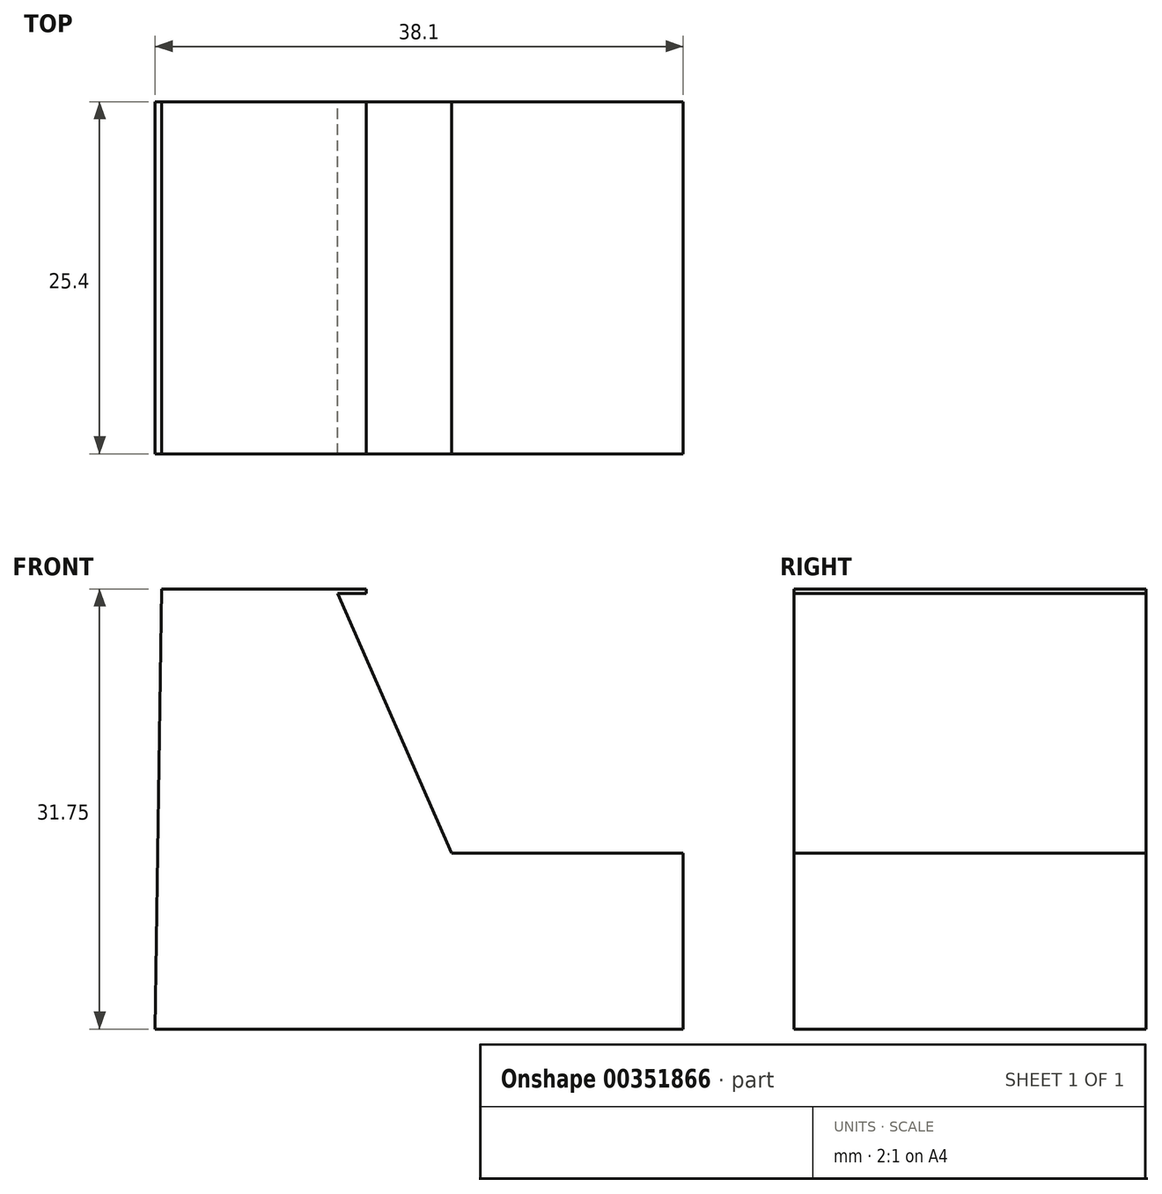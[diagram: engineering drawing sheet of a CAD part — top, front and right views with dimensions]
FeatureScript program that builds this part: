
annotation { "Feature Type Name" : "Feature", "Feature Type Description" : "" }
export const myFeature = defineFeature(function(context is Context, id is Id, definition is map)
    precondition{}
    {
        {
            var Q0;
            Q0=qCreatedBy(makeId("Front.planeOp"),FACE);
            var sketch = newSketch(context, id + "F0", { "sketchPlane" : qUnion([Q0])});
            skLineSegment(sketch, "E0", {"start": v(-38.1, 0) * mm, "end": v(0, 0) * mm});
            skLineSegment(sketch, "E1", {"start": v(0, 0) * mm, "end": v(0, 31.75) * mm});
            skLineSegment(sketch, "E2", {"start": v(0, 31.75) * mm, "end": v(-37.63, 31.75) * mm});
            skLineSegment(sketch, "E3", {"start": v(-37.63, 31.75) * mm, "end": v(-38.1, 0) * mm});
            skSolve(sketch);
        }
        {
            var Q0;
            Q0=makeQuery(id+"F0.imprint","IMPRINT",FACE,{"disambiguationData":[TD([[makeQuery(id+"F0.imprint","IMPRINT",EDGE,{"derivedFrom":sQuery(id+"F0.wireOp",EDGE,"E0")}),1.0]])]});
            var sketch = newSketch(context, id + "F1", { "sketchPlane" : qUnion([Q0])});
            skLineSegment(sketch, "E4", {"start": v(-24.93, 31.4) * mm, "end": v(-16.7, 12.7) * mm});
            skLineSegment(sketch, "E5", {"start": v(-16.7, 12.7) * mm, "end": v(0, 12.7) * mm});
            skLineSegment(sketch, "E6", {"start": v(-24.93, 31.4) * mm, "end": v(0, 31.4) * mm});
            skLineSegment(sketch, "E7", {"start": v(0, 31.4) * mm, "end": v(0, 12.7) * mm});
            skSolve(sketch);
        }
        {
            var Q0;
            Q0=makeQuery(id+"F1.imprint","IMPRINT",FACE,{"disambiguationData":[TD([[makeQuery(id+"F1.imprint","IMPRINT",EDGE,{"derivedFrom":sQuery(id+"F1.wireOp",EDGE,"E4")}),-1.0]])]});
            extrude(context, id + "F2", {"entities" : qUnion([Q0]), "depth" : 25.4 * mm});
        }
        {
            var Q0;
            Q0=makeQuery(id+"F2.opExtrude","SWEPT_FACE",FACE,{"disambiguationData":[OSD([sQuery(id+"F0.wireOp",EDGE,"E2")])]});
            var sketch = newSketch(context, id + "F3", { "sketchPlane" : qUnion([Q0])});
            skLineSegment(sketch, "E8", {"start": v(-22.86, 0) * mm, "end": v(-22.86, -35.47) * mm});
            skLineSegment(sketch, "E9", {"start": v(-22.86, 0) * mm, "end": v(0, 0) * mm});
            skLineSegment(sketch, "E10", {"start": v(0, 0) * mm, "end": v(0, -28.09) * mm});
            skLineSegment(sketch, "E11", {"start": v(-22.86, -25.4) * mm, "end": v(0, -25.4) * mm});
            skPoint(sketch, "E11.startSnap0", {"position": v(-18.81, -25.4) * mm});
            skSolve(sketch);
        }
        {
            var Q0;
            {var subQ0=sQuery(id+"F3.wireOp",EDGE,"E9");Q0=makeQuery(id+"F3.imprint","IMPRINT",FACE,{"disambiguationData":[TD([[makeQuery(id+"F3.imprint","IMPRINT",EDGE,{"derivedFrom":subQ0}),1.0]])]});}
            extrude(context, id + "F4", {"entities" : qUnion([Q0]), "operationType" : NewBodyOperationType.REMOVE, "oppositeDirection" : true, "depth" : 2.54 * mm});
        }
    });
